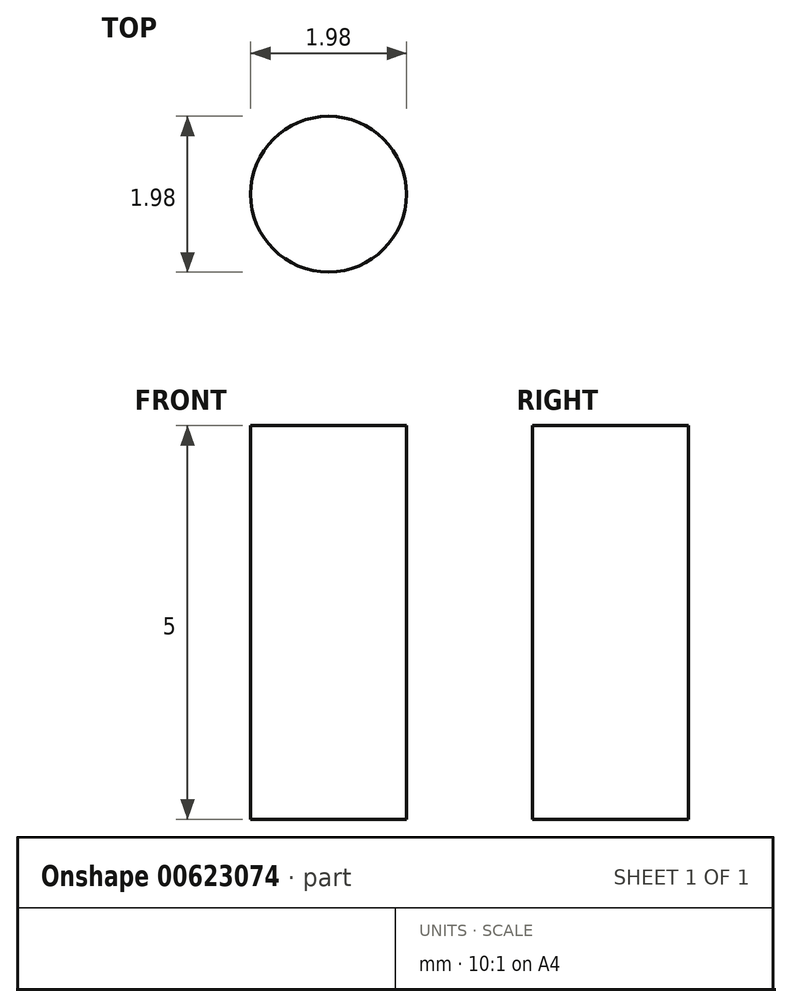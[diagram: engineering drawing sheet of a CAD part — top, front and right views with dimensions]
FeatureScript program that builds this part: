
annotation { "Feature Type Name" : "Feature", "Feature Type Description" : "" }
export const myFeature = defineFeature(function(context is Context, id is Id, definition is map)
    precondition{}
    {
        {
            var Q0;
            Q0=qCreatedBy(makeId("Top.planeOp"),FACE);
            var sketch = newSketch(context, id + "F0", { "sketchPlane" : qUnion([Q0])});
            skCircle(sketch, "E0", {"center": v(0, 0) * mm, "radius": 0.99 * mm});
            skSolve(sketch);
        }
        {
            var Q0;
            Q0=makeQuery(id+"F0.imprint","IMPRINT",FACE,{"disambiguationData":[TD([[makeQuery(id+"F0.imprint","IMPRINT",EDGE,{"derivedFrom":sQuery(id+"F0.wireOp",EDGE,"E0")}),1.0]])]});
            extrude(context, id + "F1", {"entities" : qUnion([Q0]), "depth" : -5 * mm, "offsetDistance" : 25 * mm});
        }
    });
